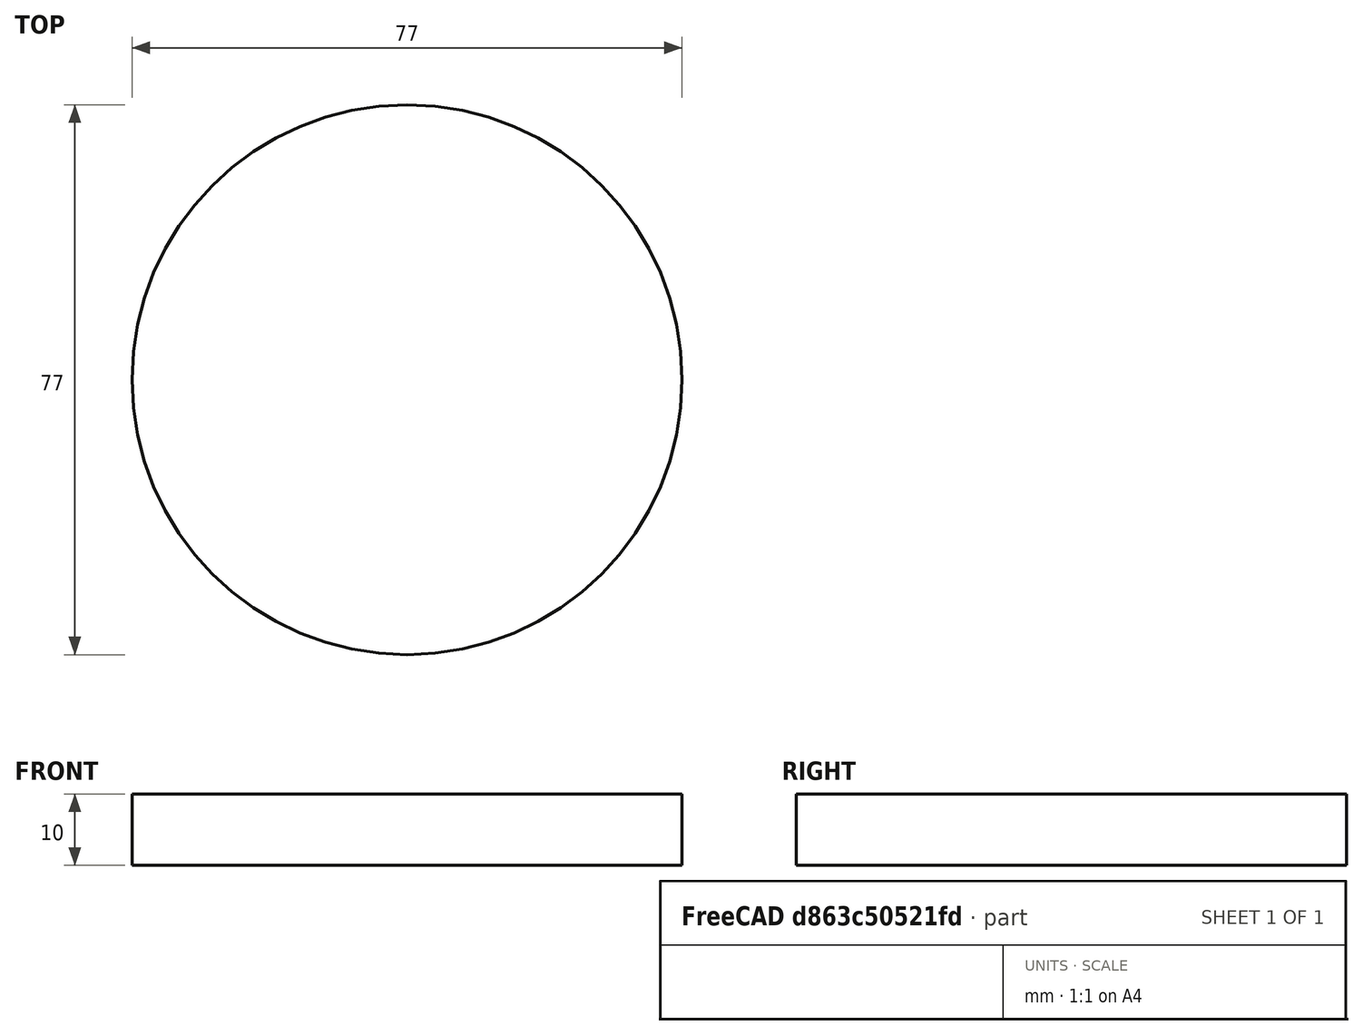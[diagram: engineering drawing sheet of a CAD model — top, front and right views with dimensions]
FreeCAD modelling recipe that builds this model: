
FCSTD DOCUMENT  (FreeCAD 1.1R14555 (Git shallow))
Label: 77mm 10mm bottom
License: All rights reserved
LicenseURL: https://en.wikipedia.org/wiki/All_rights_reserved
objects: PartDesign::Body×2, App::Point×2, Sketcher::SketchObject×1, PartDesign::Pad×1
note: 7 computed .brp shape members not serialized (recipe doc carries the construction recipe); baked Part::Feature solids carry a one-line shape summary decoded from their .brp

FEATURE [PartDesign::Body] Body
  AllowCompound = false
  Origin = -> Origin
FEATURE [App::Point] Origin001
  Role = Origin
FEATURE [App::Point] Origin003
  Role = Origin
FEATURE [Sketcher::SketchObject] Sketch
  ArcFitTolerance = 1e-06
  AttachmentSupport = -> [Origin002]
  ExternalTypes = [0]
  FullyConstrained = true
  MakeInternals = false
  MapMode = 5
  sketch-geometry (1):
    g0: Circle CenterX=0 CenterY=0 CenterZ=0 NormalX=0 NormalY=0 NormalZ=1 AngleXU=0 Radius=38.5
  constraints (2):
    c: Coincident(g0,g-1)
    c: Diameter(g0) = 77
FEATURE [PartDesign::Pad] Pad
  Direction = (0,0,1)
  Length = 10
  Length2 = 10
  Profile = -> Sketch
  ReferenceAxis = -> Sketch [N_Axis]
  SideType = 0
  Suppressed = false
  Type = 0
  Type2 = 0
FEATURE [PartDesign::Body] Body001
  AllowCompound = false
  Group = -> [Sketch,Pad]
  Origin = -> Origin002
  Tip = -> Pad
